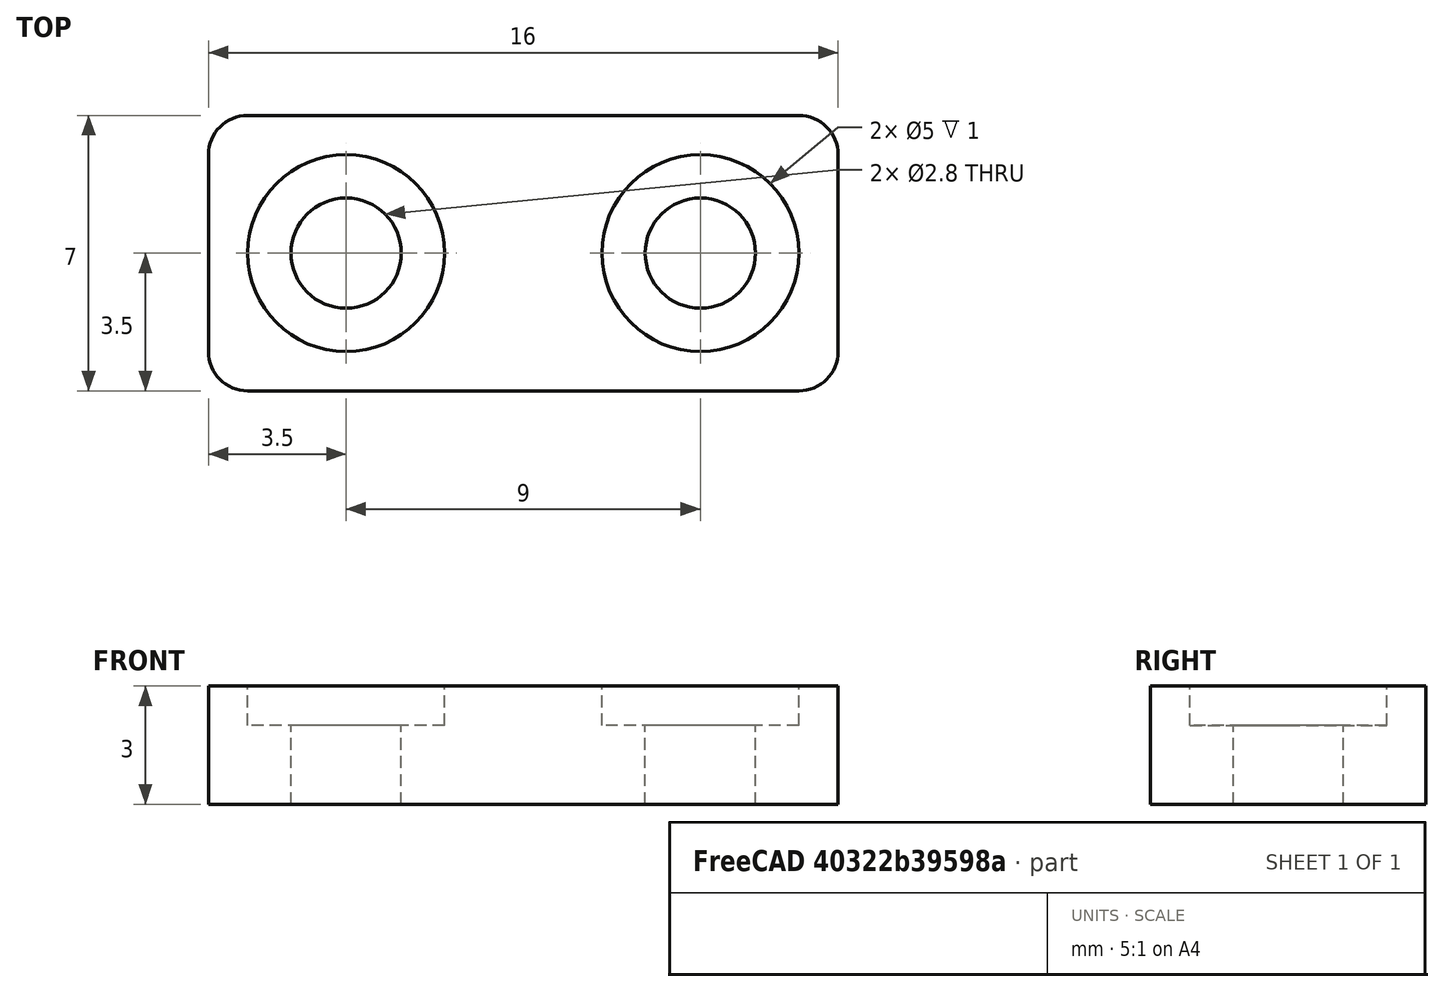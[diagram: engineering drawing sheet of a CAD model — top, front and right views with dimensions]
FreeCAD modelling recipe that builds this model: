
FCSTD DOCUMENT  (FreeCAD 0.15R4671 (Git))
Label: tendon_strap
License: All rights reserved
LicenseURL: http://en.wikipedia.org/wiki/All_rights_reserved
objects: Part::Cylinder×4, Part::Box×1, Part::MultiFuse×1, Part::Cut×1, Part::Fillet×1
note: 8 computed .brp shape members not serialized (recipe doc carries the construction recipe); baked Part::Feature solids carry a one-line shape summary decoded from their .brp

FEATURE [Part::Box] Box  label="Cube"
  Height = 3
  Length = 16
  Width = 7
FEATURE [Part::Cylinder] Cylinder
  Angle = 360
  Height = 10
  Placement = pos=(3.5,3.5,-2) rot=(0,0,1;0rad)
  Radius = 1.4
FEATURE [Part::Cylinder] Cylinder001
  Angle = 360
  Height = 10
  Placement = pos=(12.5,3.5,-2) rot=(0,0,1;0rad)
  Radius = 1.4
FEATURE [Part::Cylinder] Cylinder002
  Angle = 360
  Height = 10
  Placement = pos=(3.5,3.5,2) rot=(0,0,1;0rad)
  Radius = 2.5
FEATURE [Part::Cylinder] Cylinder003
  Angle = 360
  Height = 10
  Placement = pos=(12.5,3.5,2) rot=(0,0,1;0rad)
  Radius = 2.5
FEATURE [Part::MultiFuse] Fusion
  Shapes = -> [Cylinder,Cylinder001,Cylinder002,Cylinder003]
FEATURE [Part::Cut] Cut
  Base = -> Box
  Tool = -> Fusion
FEATURE [Part::Fillet] Fillet
  Base = -> Cut
  Edges = 4 edges r=1: [Edge1,Edge3,Edge6,Edge13]
